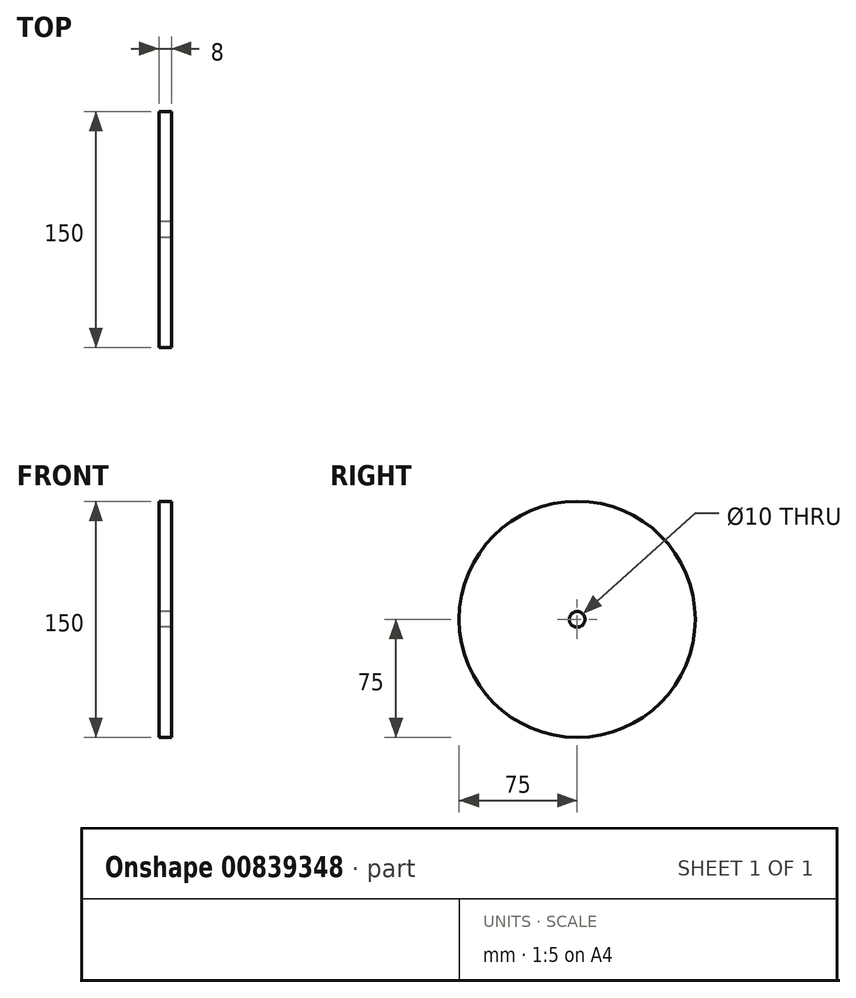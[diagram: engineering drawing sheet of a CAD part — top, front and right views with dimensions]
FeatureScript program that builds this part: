
annotation { "Feature Type Name" : "Feature", "Feature Type Description" : "" }
export const myFeature = defineFeature(function(context is Context, id is Id, definition is map)
    precondition{}
    {
        {
            var Q0;
            Q0=qCreatedBy(makeId("Right.planeOp"),FACE);
            var sketch = newSketch(context, id + "F0", { "sketchPlane" : qUnion([Q0])});
            skCircle(sketch, "E0", {"center": v(0, 0) * mm, "radius": 75 * mm});
            skCircle(sketch, "E1", {"center": v(0, 0) * mm, "radius": 5 * mm});
            skSolve(sketch);
        }
        {
            var Q0;
            Q0 = qSketchRegion(id + "F0", true);
            extrude(context, id + "F1", {"entities" : qUnion([Q0]), "depth" : 8 * mm, "offsetDistance" : 25 * mm});
        }
    });
